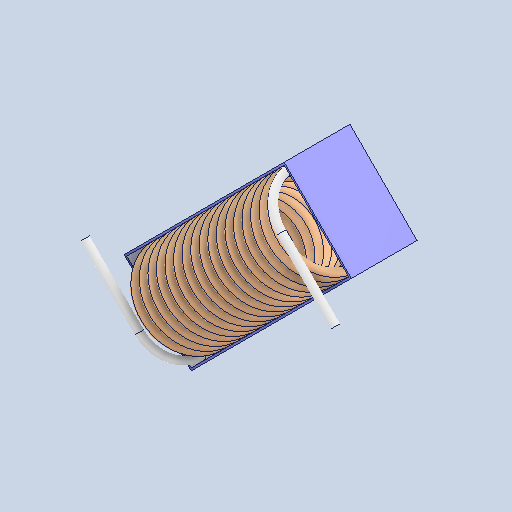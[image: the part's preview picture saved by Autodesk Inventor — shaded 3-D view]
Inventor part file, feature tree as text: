
AUTODESK INVENTOR PART (.ipt)
format: ipt  version: 2025 (Build 290162000, 162)  size: 714,240 bytes
history: native  units: mm
features: sweep x1, other x1
ambient origin geometry x8: Origin, YZ Plane, XZ Plane, XY Plane, X Axis, Y Axis, Z Axis, Center Point
bodies: Solid1 (feature_tree), Solid2 (feature_tree)
feature tree (2):
  sweep  "Sweep9"
  other  "Cut-Extrude1"
